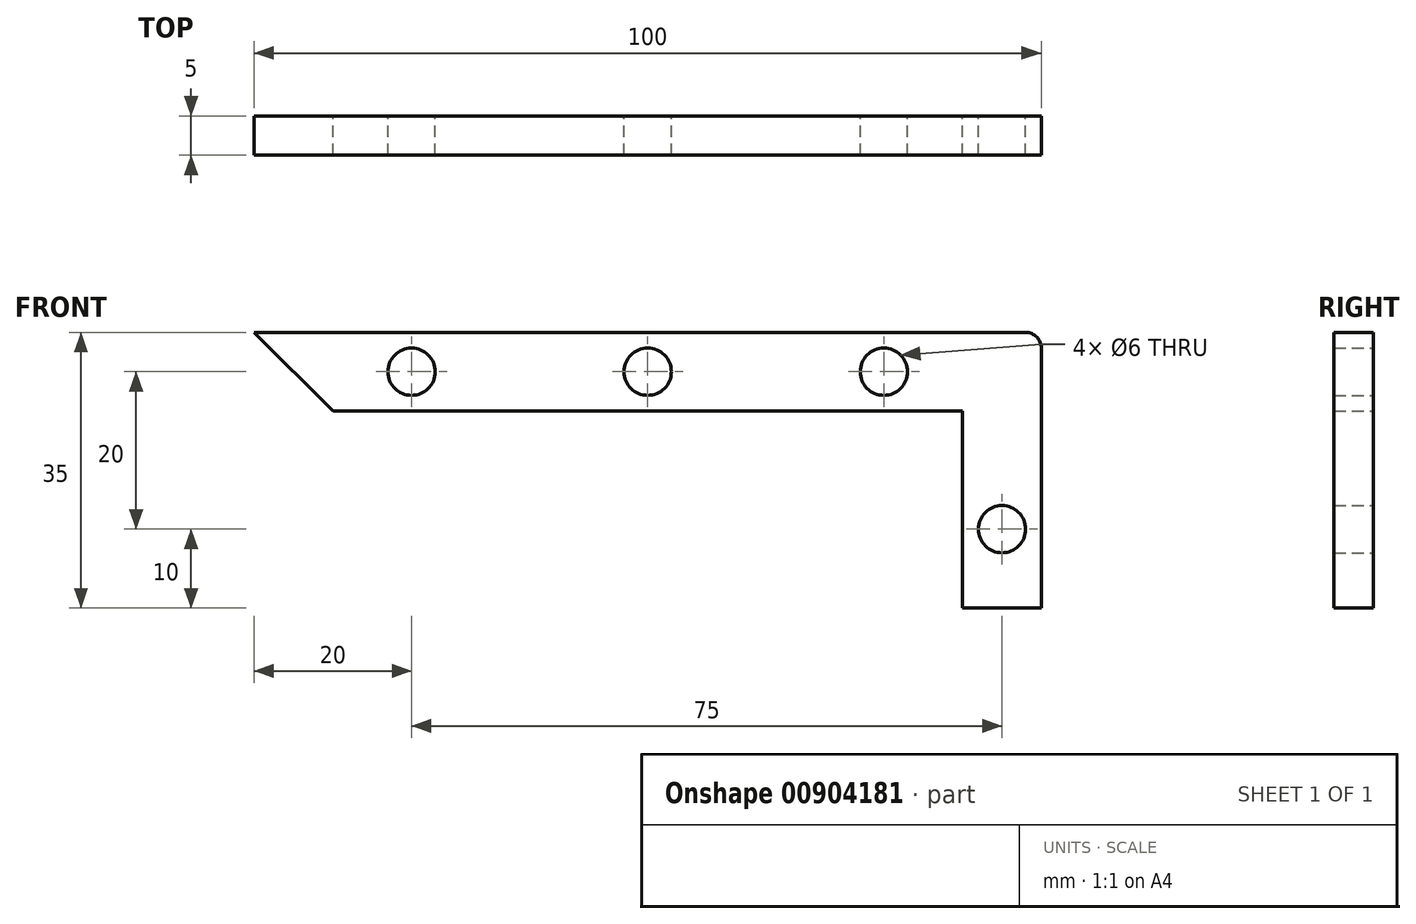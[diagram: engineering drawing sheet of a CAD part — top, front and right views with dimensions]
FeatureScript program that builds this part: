
annotation { "Feature Type Name" : "Feature", "Feature Type Description" : "" }
export const myFeature = defineFeature(function(context is Context, id is Id, definition is map)
    precondition{}
    {
        {
            var Q0;
            Q0=qCreatedBy(makeId("Front.planeOp"),FACE);
            var sketch = newSketch(context, id + "F0", { "sketchPlane" : qUnion([Q0])});
            skLineSegment(sketch, "E0.top", {"start": v(40, -19) * mm, "end": v(50, -19) * mm});
            skLineSegment(sketch, "E0.right", {"start": v(50, 14) * mm, "end": v(50, -19) * mm});
            skPoint(sketch, "E0.middle", {"position": v(0, 0) * mm});
            skPoint(sketch, "E1", {"position": v(-50, 16) * mm});
            skPoint(sketch, "E2", {"position": v(-40, 6) * mm});
            skLineSegment(sketch, "E3", {"start": v(-50, 16) * mm, "end": v(-40, 6) * mm});
            skPoint(sketch, "E4", {"position": v(48, 14) * mm});
            skArc(sketch, "E5", {"start": v(50, 14) * mm, "mid": v(49.41, 15.41) * mm, "end": v(48, 16) * mm});
            skPoint(sketch, "E6", {"position": v(-30, 11) * mm});
            skPoint(sketch, "E7", {"position": v(0, 11) * mm});
            skPoint(sketch, "E8", {"position": v(30, 11) * mm});
            skCircle(sketch, "E9", {"center": v(-30, 11) * mm, "radius": 3 * mm});
            skCircle(sketch, "E10", {"center": v(0, 11) * mm, "radius": 3 * mm});
            skCircle(sketch, "E11", {"center": v(30, 11) * mm, "radius": 3 * mm});
            skPoint(sketch, "E12", {"position": v(45, -9) * mm});
            skCircle(sketch, "E13", {"center": v(45, -9) * mm, "radius": 3 * mm});
            skLineSegment(sketch, "E14.bottom", {"start": v(-40, 6) * mm, "end": v(40, 6) * mm});
            skLineSegment(sketch, "E14.right", {"start": v(40, 6) * mm, "end": v(40, -19) * mm});
            skLineSegment(sketch, "E15", {"start": v(-50, 16) * mm, "end": v(48, 16) * mm});
            skSolve(sketch);
        }
        {
            var Q0;
            Q0 = qSketchRegion(id + "F0", true);
            extrude(context, id + "F1", {"entities" : qUnion([Q0]), "depth" : 5 * mm, "offsetDistance" : 25 * mm});
        }
    });
